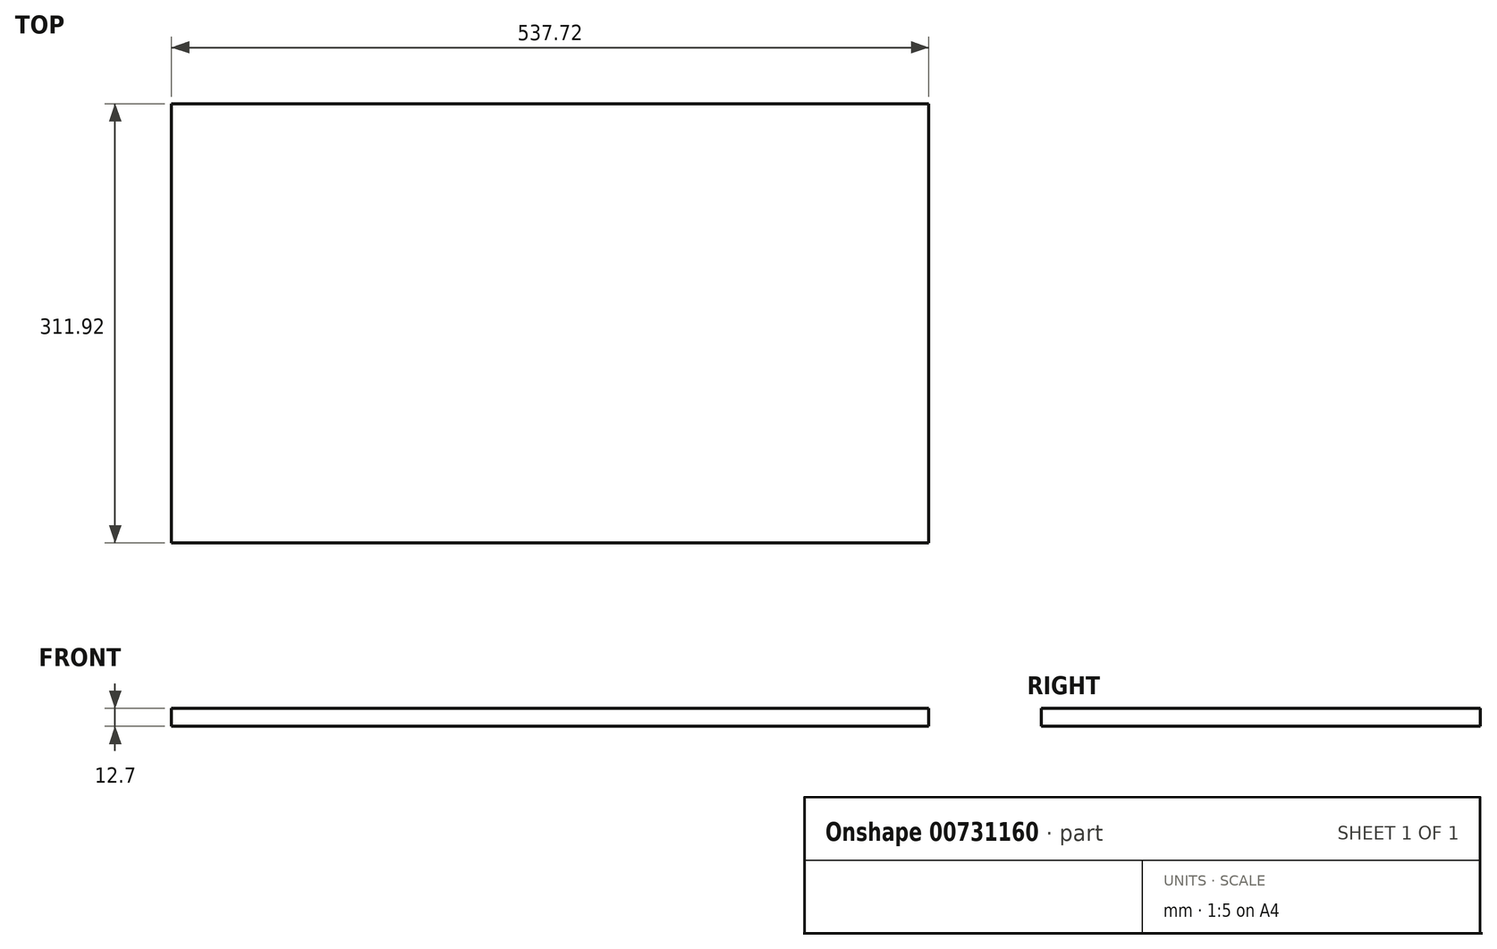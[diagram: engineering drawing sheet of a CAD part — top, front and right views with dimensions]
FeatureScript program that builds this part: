
annotation { "Feature Type Name" : "Feature", "Feature Type Description" : "" }
export const myFeature = defineFeature(function(context is Context, id is Id, definition is map)
    precondition{}
    {
        {
            var Q0;
            Q0=qCreatedBy(makeId("Top.planeOp"),FACE);
            var sketch = newSketch(context, id + "F0", { "sketchPlane" : qUnion([Q0])});
            skLineSegment(sketch, "E0.bottom", {"start": v(268.86, 155.96) * mm, "end": v(-268.86, 155.96) * mm});
            skLineSegment(sketch, "E0.top", {"start": v(268.86, -155.96) * mm, "end": v(-268.86, -155.96) * mm});
            skLineSegment(sketch, "E0.left", {"start": v(268.86, 155.96) * mm, "end": v(268.86, -155.96) * mm});
            skLineSegment(sketch, "E0.right", {"start": v(-268.86, 155.96) * mm, "end": v(-268.86, -155.96) * mm});
            skPoint(sketch, "E0.middle", {"position": v(0, 0) * mm});
            skSolve(sketch);
        }
        {
            var Q0;
            Q0 = qSketchRegion(id + "F0", true);
            extrude(context, id + "F1", {"entities" : qUnion([Q0]), "depth" : 12.7 * mm, "offsetDistance" : 25.4 * mm});
        }
    });
